# Revit family: M_灑水頭 - 直立
name_source: partatom
category: Sprinklers
revit_build: Autodesk Revit 2017 (Build: 20160109_1515(x64)
units: mm (PartAtom-declared; Revit-internal decimal feet)

## family parameters
Always vertical = Yes
Cut with Voids When Loaded = No
Maintain Annotation Orientation = Yes
OmniClass Number = 23.65.70.17.11.24
OmniClass Title = Fire Fighting Sprinkler Heads
Part Type = Normal
Room Calculation Point = No
Round Connector Dimension = Use Radius
Shared = No
Work Plane-Based = No

## types (8) — shared parameters
Coverage = Standard
Orifice = Standard
Pressure Class = Standard
Response = Standard
Temperature Rating = 57 °C

## per-type parameters (varying)
| type | CEL | K-Factor | Orifice Size | 整體長度 | 標稱直徑 | 標稱直徑半徑 |
| 15 mm 直立 | 7 mm | 81 | 13 mm | 60 mm | 15 mm | 8 mm |
| 15 mm 直立支狀 | 7 mm | 81 | 13 mm | 60 mm | 15 mm | 8 mm |
| 15 mm 直立支狀帶托架 | 7 mm | 81 | 13 mm | 60 mm | 15 mm | 8 mm |
| 15 mm 直立帶托架 | 7 mm | 81 | 13 mm | 60 mm | 15 mm | 8 mm |
| 20 mm 直立 | 10 mm | 115 | 14 mm | 64 mm | 20 mm | 10 mm |
| 20 mm 直立支狀 | 10 mm | 115 | 14 mm | 64 mm | 20 mm | 10 mm |
| 20 mm 直立支狀帶托架 | 10 mm | 115 | 14 mm | 64 mm | 20 mm | 10 mm |
| 20 mm 直立帶托架 | 10 mm | 115 | 14 mm | 64 mm | 20 mm | 10 mm |

## geometry (parser evidence)
native form markers: Sweep x1
no freeform markers — native parametric forms only
